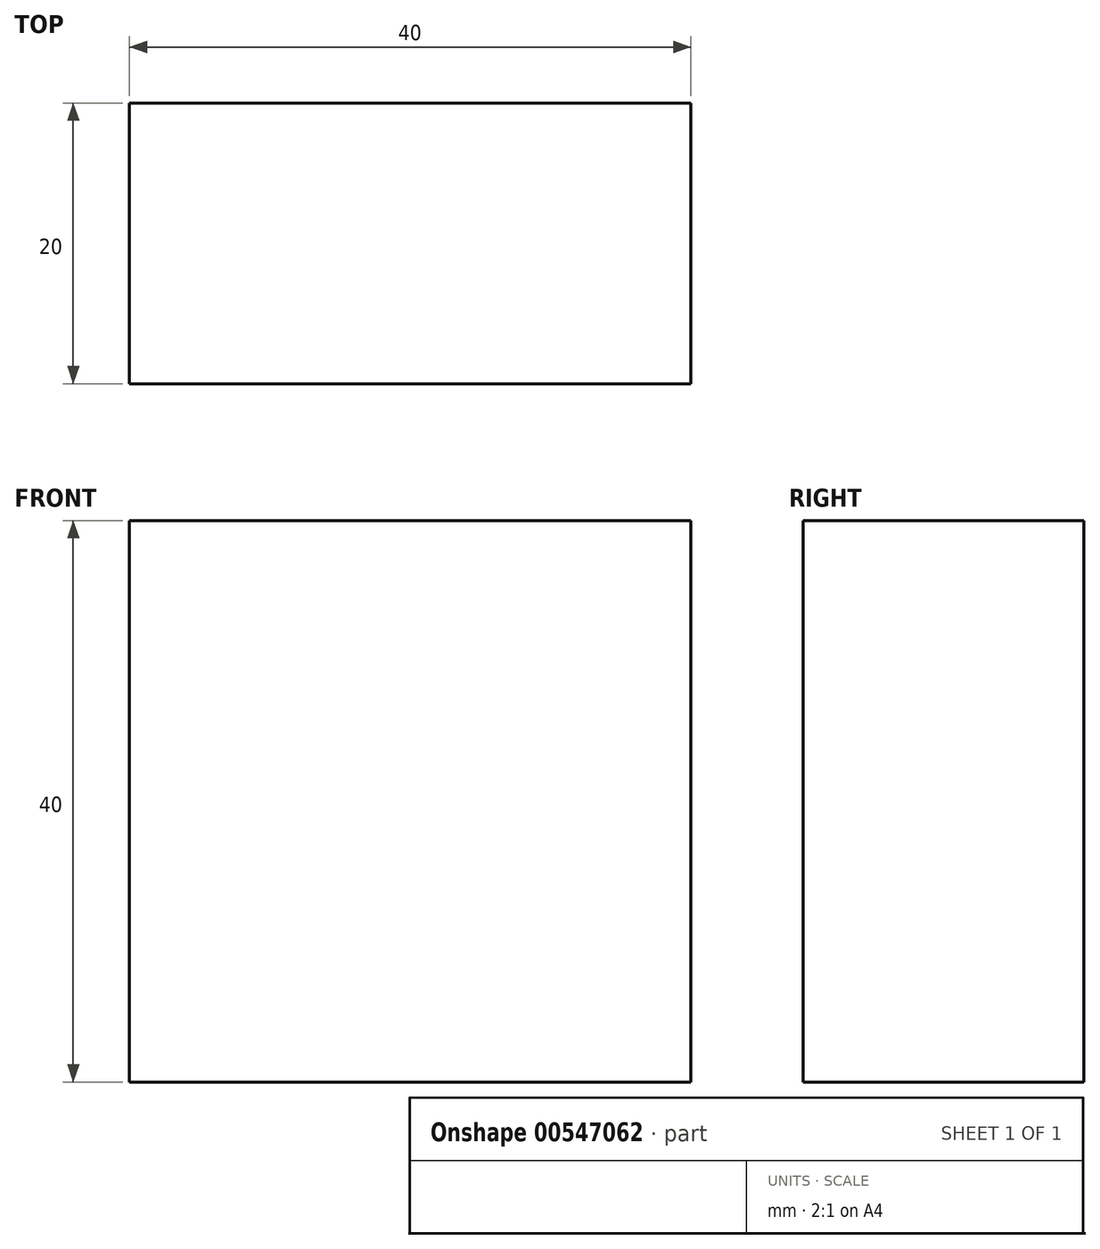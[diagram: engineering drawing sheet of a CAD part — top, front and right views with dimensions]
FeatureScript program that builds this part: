
annotation { "Feature Type Name" : "Feature", "Feature Type Description" : "" }
export const myFeature = defineFeature(function(context is Context, id is Id, definition is map)
    precondition{}
    {
        {
            var Q0;
            Q0=qCreatedBy(makeId("Top.planeOp"),FACE);
            var sketch = newSketch(context, id + "F0", { "sketchPlane" : qUnion([Q0])});
            skLineSegment(sketch, "E0.bottom", {"start": v(0, 0) * mm, "end": v(40, 0) * mm});
            skLineSegment(sketch, "E0.top", {"start": v(0, 20) * mm, "end": v(40, 20) * mm});
            skLineSegment(sketch, "E0.left", {"start": v(0, 0) * mm, "end": v(0, 20) * mm});
            skLineSegment(sketch, "E0.right", {"start": v(40, 0) * mm, "end": v(40, 20) * mm});
            skSolve(sketch);
        }
        {
            var Q0;
            Q0 = qSketchRegion(id + "F0", true);
            extrude(context, id + "F1", {"entities" : qUnion([Q0]), "depth" : 40 * mm, "offsetDistance" : 25 * mm});
        }
    });
